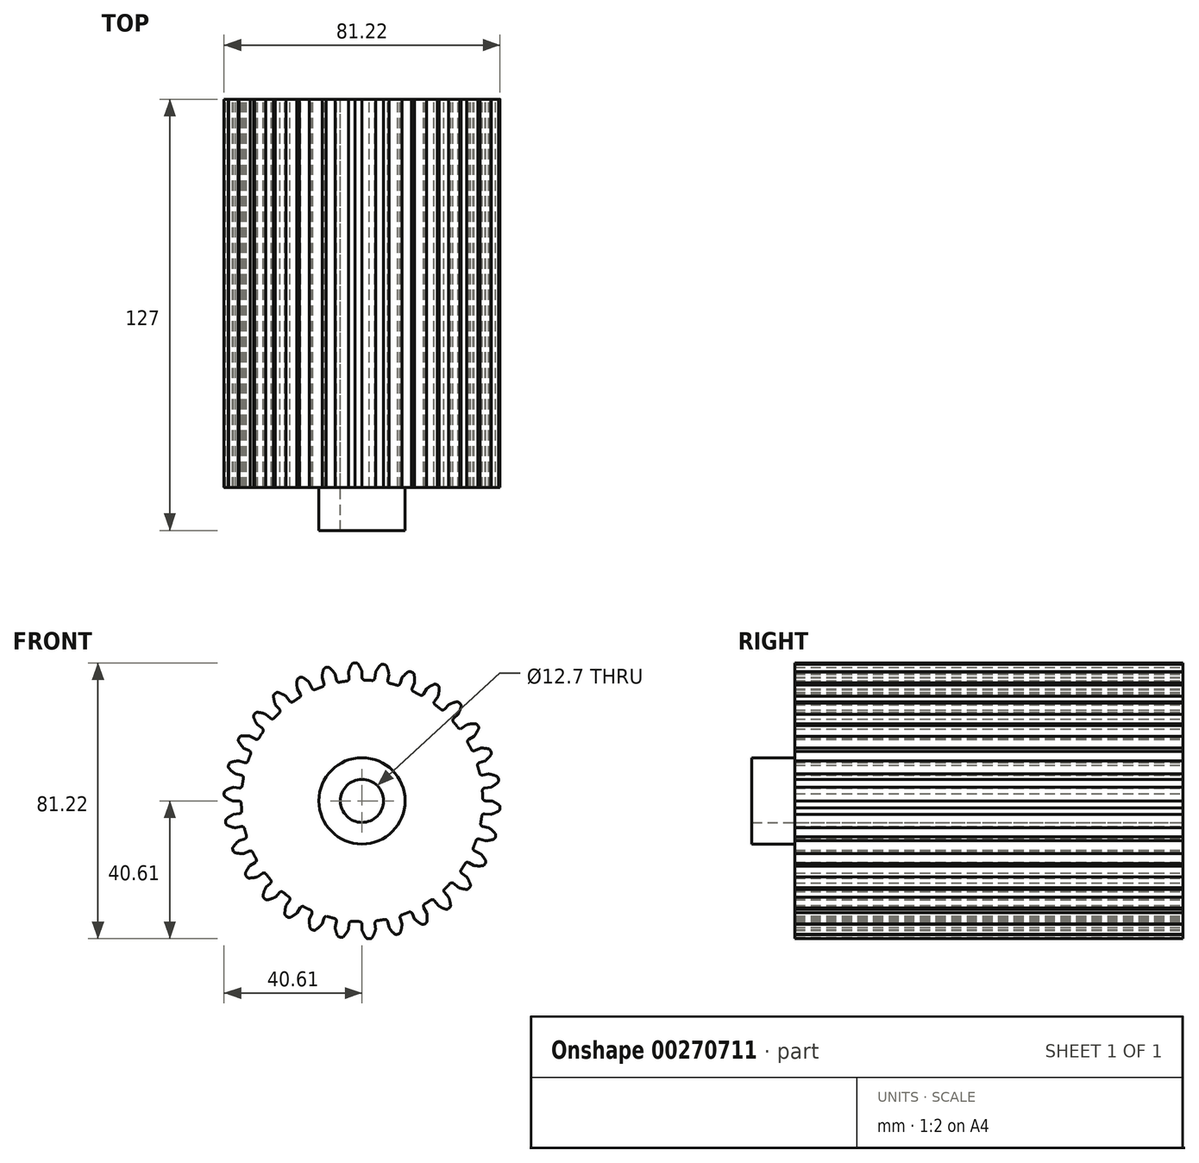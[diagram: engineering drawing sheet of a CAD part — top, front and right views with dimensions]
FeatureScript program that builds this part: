
annotation { "Feature Type Name" : "Feature", "Feature Type Description" : "" }
export const myFeature = defineFeature(function(context is Context, id is Id, definition is map)
    precondition{}
    {
        {
            var Q0;
            Q0=qCreatedBy(makeId("Front.planeOp"),FACE);
            var sketch = newSketch(context, id + "F0", { "sketchPlane" : qUnion([Q0])});
            skArc(sketch, "E0", {"start": v(-4.5, 35.28) * mm, "mid": v(-5.56, 35.12) * mm, "end": v(-6.63, 34.94) * mm});
            skArc(sketch, "E1.trimOffspring", {"start": v(0, 38.1) * mm, "mid": v(-0.52, 39.23) * mm, "end": v(-1.18, 40.3) * mm});
            skLineSegment(sketch, "E2", {"start": v(-1.82, 40.61) * mm, "end": v(-2.13, 40.61) * mm});
            skLineSegment(sketch, "E3", {"start": v(0, 38.1) * mm, "end": v(0, 36.34) * mm});
            skLineSegment(sketch, "E4.MirrorCS", {"start": v(-2.44, 40.58) * mm, "end": v(-2.13, 40.61) * mm});
            skArc(sketch, "E5.MirrorCS", {"start": v(-4, 37.9) * mm, "mid": v(-3.59, 39.07) * mm, "end": v(-3.03, 40.2) * mm});
            skLineSegment(sketch, "E6.MirrorCS", {"start": v(-4, 37.9) * mm, "end": v(-3.8, 36.14) * mm});
            skPoint(sketch, "E7.visualSharp", {"position": v(0, 35.56) * mm});
            skArc(sketch, "E7.filletArc", {"start": v(0, 36.34) * mm, "mid": v(0.23, 35.79) * mm, "end": v(0.78, 35.55) * mm});
            skPoint(sketch, "E8.visualSharp", {"position": v(-1.43, 40.61) * mm});
            skArc(sketch, "E8.filletArc", {"start": v(-1.18, 40.3) * mm, "mid": v(-1.46, 40.53) * mm, "end": v(-1.82, 40.61) * mm});
            skPoint(sketch, "E9.visualSharp", {"position": v(-2.82, 40.54) * mm});
            skArc(sketch, "E9.filletArc", {"start": v(-2.44, 40.58) * mm, "mid": v(-2.78, 40.46) * mm, "end": v(-3.03, 40.2) * mm});
            skPoint(sketch, "E10.visualSharp", {"position": v(-3.73, 35.36) * mm});
            skArc(sketch, "E10.filletArc", {"start": v(-4.5, 35.28) * mm, "mid": v(-3.97, 35.57) * mm, "end": v(-3.8, 36.14) * mm});
            skArc(sketch, "E11.1.0", {"start": v(-11.73, 33.57) * mm, "mid": v(-11.28, 33.96) * mm, "end": v(-11.24, 34.56) * mm});
            skLineSegment(sketch, "E11.1.1", {"start": v(-11.78, 36.23) * mm, "end": v(-11.24, 34.56) * mm});
            skArc(sketch, "E11.1.2", {"start": v(-11.78, 36.23) * mm, "mid": v(-11.63, 37.47) * mm, "end": v(-11.33, 38.68) * mm});
            skArc(sketch, "E11.1.3", {"start": v(-10.82, 39.19) * mm, "mid": v(-11.13, 39) * mm, "end": v(-11.33, 38.68) * mm});
            skLineSegment(sketch, "E11.1.4", {"start": v(-10.82, 39.19) * mm, "end": v(-10.53, 39.28) * mm});
            skLineSegment(sketch, "E11.1.5", {"start": v(-10.22, 39.35) * mm, "end": v(-10.53, 39.28) * mm});
            skArc(sketch, "E11.1.6", {"start": v(-9.53, 39.16) * mm, "mid": v(-9.86, 39.34) * mm, "end": v(-10.22, 39.35) * mm});
            skArc(sketch, "E11.1.7", {"start": v(-7.91, 37.27) * mm, "mid": v(-8.66, 38.27) * mm, "end": v(-9.53, 39.16) * mm});
            skLineSegment(sketch, "E11.1.8", {"start": v(-7.91, 37.27) * mm, "end": v(-7.55, 35.55) * mm});
            skArc(sketch, "E11.1.9", {"start": v(-7.55, 35.55) * mm, "mid": v(-7.21, 35.05) * mm, "end": v(-6.63, 34.94) * mm});
            skArc(sketch, "E11.2.0", {"start": v(-18.45, 30.4) * mm, "mid": v(-18.1, 30.88) * mm, "end": v(-18.18, 31.47) * mm});
            skLineSegment(sketch, "E11.2.1", {"start": v(-19.06, 33) * mm, "end": v(-18.18, 31.47) * mm});
            skArc(sketch, "E11.2.2", {"start": v(-19.06, 33) * mm, "mid": v(-19.17, 34.24) * mm, "end": v(-19.12, 35.48) * mm});
            skArc(sketch, "E11.2.3", {"start": v(-18.73, 36.08) * mm, "mid": v(-19, 35.83) * mm, "end": v(-19.12, 35.48) * mm});
            skLineSegment(sketch, "E11.2.4", {"start": v(-18.73, 36.08) * mm, "end": v(-18.46, 36.24) * mm});
            skLineSegment(sketch, "E11.2.5", {"start": v(-18.18, 36.36) * mm, "end": v(-18.46, 36.24) * mm});
            skArc(sketch, "E11.2.6", {"start": v(-17.47, 36.33) * mm, "mid": v(-17.82, 36.43) * mm, "end": v(-18.18, 36.36) * mm});
            skArc(sketch, "E11.2.7", {"start": v(-15.49, 34.8) * mm, "mid": v(-16.43, 35.63) * mm, "end": v(-17.47, 36.33) * mm});
            skLineSegment(sketch, "E11.2.8", {"start": v(-15.49, 34.8) * mm, "end": v(-14.77, 33.2) * mm});
            skArc(sketch, "E11.2.9", {"start": v(-14.77, 33.2) * mm, "mid": v(-14.34, 32.79) * mm, "end": v(-13.75, 32.8) * mm});
            skArc(sketch, "E11.3.0", {"start": v(-24.37, 25.9) * mm, "mid": v(-24.12, 26.44) * mm, "end": v(-24.32, 27) * mm});
            skLineSegment(sketch, "E11.3.1", {"start": v(-25.5, 28.3) * mm, "end": v(-24.32, 27) * mm});
            skArc(sketch, "E11.3.2", {"start": v(-25.5, 28.3) * mm, "mid": v(-25.87, 29.5) * mm, "end": v(-26.08, 30.73) * mm});
            skArc(sketch, "E11.3.3", {"start": v(-25.82, 31.4) * mm, "mid": v(-26.03, 31.1) * mm, "end": v(-26.08, 30.73) * mm});
            skLineSegment(sketch, "E11.3.4", {"start": v(-25.82, 31.4) * mm, "end": v(-25.6, 31.6) * mm});
            skLineSegment(sketch, "E11.3.5", {"start": v(-25.34, 31.79) * mm, "end": v(-25.6, 31.6) * mm});
            skArc(sketch, "E11.3.6", {"start": v(-24.64, 31.9) * mm, "mid": v(-25, 31.93) * mm, "end": v(-25.34, 31.79) * mm});
            skArc(sketch, "E11.3.7", {"start": v(-22.39, 30.83) * mm, "mid": v(-23.48, 31.44) * mm, "end": v(-24.64, 31.9) * mm});
            skLineSegment(sketch, "E11.3.8", {"start": v(-22.39, 30.83) * mm, "end": v(-21.35, 29.4) * mm});
            skArc(sketch, "E11.3.9", {"start": v(-21.35, 29.4) * mm, "mid": v(-20.85, 29.1) * mm, "end": v(-20.27, 29.22) * mm});
            skArc(sketch, "E11.4.0", {"start": v(-29.22, 20.27) * mm, "mid": v(-29.1, 20.85) * mm, "end": v(-29.4, 21.35) * mm});
            skLineSegment(sketch, "E11.4.1", {"start": v(-30.83, 22.39) * mm, "end": v(-29.4, 21.35) * mm});
            skArc(sketch, "E11.4.2", {"start": v(-30.83, 22.39) * mm, "mid": v(-31.44, 23.48) * mm, "end": v(-31.9, 24.64) * mm});
            skArc(sketch, "E11.4.3", {"start": v(-31.79, 25.34) * mm, "mid": v(-31.93, 25) * mm, "end": v(-31.9, 24.64) * mm});
            skLineSegment(sketch, "E11.4.4", {"start": v(-31.79, 25.34) * mm, "end": v(-31.6, 25.6) * mm});
            skLineSegment(sketch, "E11.4.5", {"start": v(-31.4, 25.82) * mm, "end": v(-31.6, 25.6) * mm});
            skArc(sketch, "E11.4.6", {"start": v(-30.73, 26.08) * mm, "mid": v(-31.1, 26.03) * mm, "end": v(-31.4, 25.82) * mm});
            skArc(sketch, "E11.4.7", {"start": v(-28.3, 25.5) * mm, "mid": v(-29.5, 25.87) * mm, "end": v(-30.73, 26.08) * mm});
            skLineSegment(sketch, "E11.4.8", {"start": v(-28.3, 25.5) * mm, "end": v(-27, 24.32) * mm});
            skArc(sketch, "E11.4.9", {"start": v(-27, 24.32) * mm, "mid": v(-26.44, 24.12) * mm, "end": v(-25.9, 24.37) * mm});
            skArc(sketch, "E11.5.0", {"start": v(-32.8, 13.75) * mm, "mid": v(-32.79, 14.34) * mm, "end": v(-33.2, 14.77) * mm});
            skLineSegment(sketch, "E11.5.1", {"start": v(-34.8, 15.49) * mm, "end": v(-33.2, 14.77) * mm});
            skArc(sketch, "E11.5.2", {"start": v(-34.8, 15.49) * mm, "mid": v(-35.63, 16.43) * mm, "end": v(-36.33, 17.47) * mm});
            skArc(sketch, "E11.5.3", {"start": v(-36.36, 18.18) * mm, "mid": v(-36.43, 17.82) * mm, "end": v(-36.33, 17.47) * mm});
            skLineSegment(sketch, "E11.5.4", {"start": v(-36.36, 18.18) * mm, "end": v(-36.24, 18.46) * mm});
            skLineSegment(sketch, "E11.5.5", {"start": v(-36.08, 18.73) * mm, "end": v(-36.24, 18.46) * mm});
            skArc(sketch, "E11.5.6", {"start": v(-35.48, 19.12) * mm, "mid": v(-35.83, 19) * mm, "end": v(-36.08, 18.73) * mm});
            skArc(sketch, "E11.5.7", {"start": v(-33, 19.06) * mm, "mid": v(-34.24, 19.17) * mm, "end": v(-35.48, 19.12) * mm});
            skLineSegment(sketch, "E11.5.8", {"start": v(-33, 19.06) * mm, "end": v(-31.47, 18.18) * mm});
            skArc(sketch, "E11.5.9", {"start": v(-31.47, 18.18) * mm, "mid": v(-30.88, 18.1) * mm, "end": v(-30.4, 18.45) * mm});
            skArc(sketch, "E11.6.0", {"start": v(-34.94, 6.63) * mm, "mid": v(-35.05, 7.21) * mm, "end": v(-35.55, 7.55) * mm});
            skLineSegment(sketch, "E11.6.1", {"start": v(-37.27, 7.91) * mm, "end": v(-35.55, 7.55) * mm});
            skArc(sketch, "E11.6.2", {"start": v(-37.27, 7.91) * mm, "mid": v(-38.27, 8.66) * mm, "end": v(-39.16, 9.53) * mm});
            skArc(sketch, "E11.6.3", {"start": v(-39.35, 10.22) * mm, "mid": v(-39.34, 9.86) * mm, "end": v(-39.16, 9.53) * mm});
            skLineSegment(sketch, "E11.6.4", {"start": v(-39.35, 10.22) * mm, "end": v(-39.28, 10.53) * mm});
            skLineSegment(sketch, "E11.6.5", {"start": v(-39.19, 10.82) * mm, "end": v(-39.28, 10.53) * mm});
            skArc(sketch, "E11.6.6", {"start": v(-38.68, 11.33) * mm, "mid": v(-39, 11.13) * mm, "end": v(-39.19, 10.82) * mm});
            skArc(sketch, "E11.6.7", {"start": v(-36.23, 11.78) * mm, "mid": v(-37.47, 11.63) * mm, "end": v(-38.68, 11.33) * mm});
            skLineSegment(sketch, "E11.6.8", {"start": v(-36.23, 11.78) * mm, "end": v(-34.56, 11.24) * mm});
            skArc(sketch, "E11.6.9", {"start": v(-34.56, 11.24) * mm, "mid": v(-33.96, 11.28) * mm, "end": v(-33.57, 11.73) * mm});
            skArc(sketch, "E11.7.0", {"start": v(-35.55, -0.78) * mm, "mid": v(-35.79, -0.23) * mm, "end": v(-36.34, 0) * mm});
            skLineSegment(sketch, "E11.7.1", {"start": v(-38.1, 0) * mm, "end": v(-36.34, 0) * mm});
            skArc(sketch, "E11.7.2", {"start": v(-38.1, 0) * mm, "mid": v(-39.23, 0.52) * mm, "end": v(-40.3, 1.18) * mm});
            skArc(sketch, "E11.7.3", {"start": v(-40.61, 1.82) * mm, "mid": v(-40.53, 1.46) * mm, "end": v(-40.3, 1.18) * mm});
            skLineSegment(sketch, "E11.7.4", {"start": v(-40.61, 1.82) * mm, "end": v(-40.61, 2.13) * mm});
            skLineSegment(sketch, "E11.7.5", {"start": v(-40.58, 2.44) * mm, "end": v(-40.61, 2.13) * mm});
            skArc(sketch, "E11.7.6", {"start": v(-40.2, 3.03) * mm, "mid": v(-40.46, 2.78) * mm, "end": v(-40.58, 2.44) * mm});
            skArc(sketch, "E11.7.7", {"start": v(-37.9, 4) * mm, "mid": v(-39.07, 3.59) * mm, "end": v(-40.2, 3.03) * mm});
            skLineSegment(sketch, "E11.7.8", {"start": v(-37.9, 4) * mm, "end": v(-36.14, 3.8) * mm});
            skArc(sketch, "E11.7.9", {"start": v(-36.14, 3.8) * mm, "mid": v(-35.57, 3.97) * mm, "end": v(-35.28, 4.5) * mm});
            skArc(sketch, "E11.8.0", {"start": v(-34.61, -8.15) * mm, "mid": v(-34.96, -7.67) * mm, "end": v(-35.54, -7.56) * mm});
            skLineSegment(sketch, "E11.8.1", {"start": v(-37.27, -7.93) * mm, "end": v(-35.54, -7.56) * mm});
            skArc(sketch, "E11.8.2", {"start": v(-37.27, -7.93) * mm, "mid": v(-38.48, -7.65) * mm, "end": v(-39.66, -7.22) * mm});
            skArc(sketch, "E11.8.3", {"start": v(-40.1, -6.66) * mm, "mid": v(-39.95, -7) * mm, "end": v(-39.66, -7.22) * mm});
            skLineSegment(sketch, "E11.8.4", {"start": v(-40.1, -6.66) * mm, "end": v(-40.17, -6.36) * mm});
            skLineSegment(sketch, "E11.8.5", {"start": v(-40.2, -6.06) * mm, "end": v(-40.17, -6.36) * mm});
            skArc(sketch, "E11.8.6", {"start": v(-39.95, -5.39) * mm, "mid": v(-40.15, -5.7) * mm, "end": v(-40.2, -6.06) * mm});
            skArc(sketch, "E11.8.7", {"start": v(-37.9, -3.97) * mm, "mid": v(-38.97, -4.61) * mm, "end": v(-39.95, -5.39) * mm});
            skLineSegment(sketch, "E11.8.8", {"start": v(-37.9, -3.97) * mm, "end": v(-36.14, -3.79) * mm});
            skArc(sketch, "E11.8.9", {"start": v(-36.14, -3.79) * mm, "mid": v(-35.62, -3.5) * mm, "end": v(-35.44, -2.94) * mm});
            skArc(sketch, "E11.9.0", {"start": v(-32.16, -15.17) * mm, "mid": v(-32.6, -14.77) * mm, "end": v(-33.2, -14.79) * mm});
            skLineSegment(sketch, "E11.9.1", {"start": v(-34.8, -15.5) * mm, "end": v(-33.2, -14.79) * mm});
            skArc(sketch, "E11.9.2", {"start": v(-34.8, -15.5) * mm, "mid": v(-36.05, -15.49) * mm, "end": v(-37.29, -15.3) * mm});
            skArc(sketch, "E11.9.3", {"start": v(-37.84, -14.86) * mm, "mid": v(-37.62, -15.15) * mm, "end": v(-37.29, -15.3) * mm});
            skLineSegment(sketch, "E11.9.4", {"start": v(-37.84, -14.86) * mm, "end": v(-37.97, -14.58) * mm});
            skLineSegment(sketch, "E11.9.5", {"start": v(-38.06, -14.28) * mm, "end": v(-37.97, -14.58) * mm});
            skArc(sketch, "E11.9.6", {"start": v(-37.95, -13.58) * mm, "mid": v(-38.1, -13.92) * mm, "end": v(-38.06, -14.28) * mm});
            skArc(sketch, "E11.9.7", {"start": v(-36.24, -11.77) * mm, "mid": v(-37.16, -12.61) * mm, "end": v(-37.95, -13.58) * mm});
            skLineSegment(sketch, "E11.9.8", {"start": v(-36.24, -11.77) * mm, "end": v(-34.56, -11.22) * mm});
            skArc(sketch, "E11.9.9", {"start": v(-34.56, -11.22) * mm, "mid": v(-34.1, -10.84) * mm, "end": v(-34.05, -10.25) * mm});
            skArc(sketch, "E11.10.0", {"start": v(-28.3, -21.53) * mm, "mid": v(-28.82, -21.22) * mm, "end": v(-29.4, -21.37) * mm});
            skLineSegment(sketch, "E11.10.1", {"start": v(-30.82, -22.4) * mm, "end": v(-29.4, -21.37) * mm});
            skArc(sketch, "E11.10.2", {"start": v(-30.82, -22.4) * mm, "mid": v(-32.04, -22.64) * mm, "end": v(-33.3, -22.73) * mm});
            skArc(sketch, "E11.10.3", {"start": v(-33.93, -22.4) * mm, "mid": v(-33.65, -22.64) * mm, "end": v(-33.3, -22.73) * mm});
            skLineSegment(sketch, "E11.10.4", {"start": v(-33.93, -22.4) * mm, "end": v(-34.1, -22.15) * mm});
            skLineSegment(sketch, "E11.10.5", {"start": v(-34.26, -21.88) * mm, "end": v(-34.1, -22.15) * mm});
            skArc(sketch, "E11.10.6", {"start": v(-34.3, -21.17) * mm, "mid": v(-34.37, -21.53) * mm, "end": v(-34.26, -21.88) * mm});
            skArc(sketch, "E11.10.7", {"start": v(-33, -19.04) * mm, "mid": v(-33.72, -20.06) * mm, "end": v(-34.3, -21.17) * mm});
            skLineSegment(sketch, "E11.10.8", {"start": v(-33, -19.04) * mm, "end": v(-31.47, -18.16) * mm});
            skArc(sketch, "E11.10.9", {"start": v(-31.47, -18.16) * mm, "mid": v(-31.11, -17.7) * mm, "end": v(-31.18, -17.1) * mm});
            skArc(sketch, "E11.11.0", {"start": v(-23.2, -26.94) * mm, "mid": v(-23.77, -26.75) * mm, "end": v(-24.3, -27.01) * mm});
            skLineSegment(sketch, "E11.11.1", {"start": v(-25.49, -28.32) * mm, "end": v(-24.3, -27.01) * mm});
            skArc(sketch, "E11.11.2", {"start": v(-25.49, -28.32) * mm, "mid": v(-26.64, -28.81) * mm, "end": v(-27.84, -29.15) * mm});
            skArc(sketch, "E11.11.3", {"start": v(-28.53, -28.97) * mm, "mid": v(-28.2, -29.14) * mm, "end": v(-27.84, -29.15) * mm});
            skLineSegment(sketch, "E11.11.4", {"start": v(-28.53, -28.97) * mm, "end": v(-28.76, -28.76) * mm});
            skLineSegment(sketch, "E11.11.5", {"start": v(-28.97, -28.53) * mm, "end": v(-28.76, -28.76) * mm});
            skArc(sketch, "E11.11.6", {"start": v(-29.15, -27.84) * mm, "mid": v(-29.14, -28.2) * mm, "end": v(-28.97, -28.53) * mm});
            skArc(sketch, "E11.11.7", {"start": v(-28.32, -25.49) * mm, "mid": v(-28.81, -26.64) * mm, "end": v(-29.15, -27.84) * mm});
            skLineSegment(sketch, "E11.11.8", {"start": v(-28.32, -25.49) * mm, "end": v(-27.01, -24.3) * mm});
            skArc(sketch, "E11.11.9", {"start": v(-27.01, -24.3) * mm, "mid": v(-26.75, -23.77) * mm, "end": v(-26.94, -23.2) * mm});
            skArc(sketch, "E11.12.0", {"start": v(-17.1, -31.18) * mm, "mid": v(-17.7, -31.11) * mm, "end": v(-18.16, -31.47) * mm});
            skLineSegment(sketch, "E11.12.1", {"start": v(-19.04, -33) * mm, "end": v(-18.16, -31.47) * mm});
            skArc(sketch, "E11.12.2", {"start": v(-19.04, -33) * mm, "mid": v(-20.06, -33.72) * mm, "end": v(-21.17, -34.3) * mm});
            skArc(sketch, "E11.12.3", {"start": v(-21.88, -34.26) * mm, "mid": v(-21.53, -34.37) * mm, "end": v(-21.17, -34.3) * mm});
            skLineSegment(sketch, "E11.12.4", {"start": v(-21.88, -34.26) * mm, "end": v(-22.15, -34.1) * mm});
            skLineSegment(sketch, "E11.12.5", {"start": v(-22.4, -33.93) * mm, "end": v(-22.15, -34.1) * mm});
            skArc(sketch, "E11.12.6", {"start": v(-22.73, -33.3) * mm, "mid": v(-22.64, -33.65) * mm, "end": v(-22.4, -33.93) * mm});
            skArc(sketch, "E11.12.7", {"start": v(-22.4, -30.82) * mm, "mid": v(-22.64, -32.04) * mm, "end": v(-22.73, -33.3) * mm});
            skLineSegment(sketch, "E11.12.8", {"start": v(-22.4, -30.82) * mm, "end": v(-21.37, -29.4) * mm});
            skArc(sketch, "E11.12.9", {"start": v(-21.37, -29.4) * mm, "mid": v(-21.22, -28.82) * mm, "end": v(-21.53, -28.3) * mm});
            skArc(sketch, "E11.13.0", {"start": v(-10.25, -34.05) * mm, "mid": v(-10.84, -34.1) * mm, "end": v(-11.22, -34.56) * mm});
            skLineSegment(sketch, "E11.13.1", {"start": v(-11.77, -36.24) * mm, "end": v(-11.22, -34.56) * mm});
            skArc(sketch, "E11.13.2", {"start": v(-11.77, -36.24) * mm, "mid": v(-12.61, -37.16) * mm, "end": v(-13.58, -37.95) * mm});
            skArc(sketch, "E11.13.3", {"start": v(-14.28, -38.06) * mm, "mid": v(-13.92, -38.1) * mm, "end": v(-13.58, -37.95) * mm});
            skLineSegment(sketch, "E11.13.4", {"start": v(-14.28, -38.06) * mm, "end": v(-14.58, -37.97) * mm});
            skLineSegment(sketch, "E11.13.5", {"start": v(-14.86, -37.84) * mm, "end": v(-14.58, -37.97) * mm});
            skArc(sketch, "E11.13.6", {"start": v(-15.3, -37.29) * mm, "mid": v(-15.15, -37.62) * mm, "end": v(-14.86, -37.84) * mm});
            skArc(sketch, "E11.13.7", {"start": v(-15.5, -34.8) * mm, "mid": v(-15.49, -36.05) * mm, "end": v(-15.3, -37.29) * mm});
            skLineSegment(sketch, "E11.13.8", {"start": v(-15.5, -34.8) * mm, "end": v(-14.79, -33.2) * mm});
            skArc(sketch, "E11.13.9", {"start": v(-14.79, -33.2) * mm, "mid": v(-14.77, -32.6) * mm, "end": v(-15.17, -32.16) * mm});
            skArc(sketch, "E11.14.0", {"start": v(-2.94, -35.44) * mm, "mid": v(-3.5, -35.62) * mm, "end": v(-3.79, -36.14) * mm});
            skLineSegment(sketch, "E11.14.1", {"start": v(-3.97, -37.9) * mm, "end": v(-3.79, -36.14) * mm});
            skArc(sketch, "E11.14.2", {"start": v(-3.97, -37.9) * mm, "mid": v(-4.61, -38.97) * mm, "end": v(-5.39, -39.95) * mm});
            skArc(sketch, "E11.14.3", {"start": v(-6.06, -40.2) * mm, "mid": v(-5.7, -40.15) * mm, "end": v(-5.39, -39.95) * mm});
            skLineSegment(sketch, "E11.14.4", {"start": v(-6.06, -40.2) * mm, "end": v(-6.36, -40.17) * mm});
            skLineSegment(sketch, "E11.14.5", {"start": v(-6.66, -40.1) * mm, "end": v(-6.36, -40.17) * mm});
            skArc(sketch, "E11.14.6", {"start": v(-7.22, -39.66) * mm, "mid": v(-7, -39.95) * mm, "end": v(-6.66, -40.1) * mm});
            skArc(sketch, "E11.14.7", {"start": v(-7.93, -37.27) * mm, "mid": v(-7.65, -38.48) * mm, "end": v(-7.22, -39.66) * mm});
            skLineSegment(sketch, "E11.14.8", {"start": v(-7.93, -37.27) * mm, "end": v(-7.56, -35.54) * mm});
            skArc(sketch, "E11.14.9", {"start": v(-7.56, -35.54) * mm, "mid": v(-7.67, -34.96) * mm, "end": v(-8.15, -34.61) * mm});
            skArc(sketch, "E11.15.0", {"start": v(4.5, -35.28) * mm, "mid": v(3.97, -35.57) * mm, "end": v(3.8, -36.14) * mm});
            skLineSegment(sketch, "E11.15.1", {"start": v(4, -37.9) * mm, "end": v(3.8, -36.14) * mm});
            skArc(sketch, "E11.15.2", {"start": v(4, -37.9) * mm, "mid": v(3.59, -39.07) * mm, "end": v(3.03, -40.2) * mm});
            skArc(sketch, "E11.15.3", {"start": v(2.44, -40.58) * mm, "mid": v(2.78, -40.46) * mm, "end": v(3.03, -40.2) * mm});
            skLineSegment(sketch, "E11.15.4", {"start": v(2.44, -40.58) * mm, "end": v(2.13, -40.61) * mm});
            skLineSegment(sketch, "E11.15.5", {"start": v(1.82, -40.61) * mm, "end": v(2.13, -40.61) * mm});
            skArc(sketch, "E11.15.6", {"start": v(1.18, -40.3) * mm, "mid": v(1.46, -40.53) * mm, "end": v(1.82, -40.61) * mm});
            skArc(sketch, "E11.15.7", {"start": v(0, -38.1) * mm, "mid": v(0.52, -39.23) * mm, "end": v(1.18, -40.3) * mm});
            skLineSegment(sketch, "E11.15.8", {"start": v(0, -38.1) * mm, "end": v(0, -36.34) * mm});
            skArc(sketch, "E11.15.9", {"start": v(0, -36.34) * mm, "mid": v(-0.23, -35.79) * mm, "end": v(-0.78, -35.55) * mm});
            skArc(sketch, "E11.16.0", {"start": v(11.73, -33.57) * mm, "mid": v(11.28, -33.96) * mm, "end": v(11.24, -34.56) * mm});
            skLineSegment(sketch, "E11.16.1", {"start": v(11.78, -36.23) * mm, "end": v(11.24, -34.56) * mm});
            skArc(sketch, "E11.16.2", {"start": v(11.78, -36.23) * mm, "mid": v(11.63, -37.47) * mm, "end": v(11.33, -38.68) * mm});
            skArc(sketch, "E11.16.3", {"start": v(10.82, -39.19) * mm, "mid": v(11.13, -39) * mm, "end": v(11.33, -38.68) * mm});
            skLineSegment(sketch, "E11.16.4", {"start": v(10.82, -39.19) * mm, "end": v(10.53, -39.28) * mm});
            skLineSegment(sketch, "E11.16.5", {"start": v(10.22, -39.35) * mm, "end": v(10.53, -39.28) * mm});
            skArc(sketch, "E11.16.6", {"start": v(9.53, -39.16) * mm, "mid": v(9.86, -39.34) * mm, "end": v(10.22, -39.35) * mm});
            skArc(sketch, "E11.16.7", {"start": v(7.91, -37.27) * mm, "mid": v(8.66, -38.27) * mm, "end": v(9.53, -39.16) * mm});
            skLineSegment(sketch, "E11.16.8", {"start": v(7.91, -37.27) * mm, "end": v(7.55, -35.55) * mm});
            skArc(sketch, "E11.16.9", {"start": v(7.55, -35.55) * mm, "mid": v(7.21, -35.05) * mm, "end": v(6.63, -34.94) * mm});
            skArc(sketch, "E11.17.0", {"start": v(18.45, -30.4) * mm, "mid": v(18.1, -30.88) * mm, "end": v(18.18, -31.47) * mm});
            skLineSegment(sketch, "E11.17.1", {"start": v(19.06, -33) * mm, "end": v(18.18, -31.47) * mm});
            skArc(sketch, "E11.17.2", {"start": v(19.06, -33) * mm, "mid": v(19.17, -34.24) * mm, "end": v(19.12, -35.48) * mm});
            skArc(sketch, "E11.17.3", {"start": v(18.73, -36.08) * mm, "mid": v(19, -35.83) * mm, "end": v(19.12, -35.48) * mm});
            skLineSegment(sketch, "E11.17.4", {"start": v(18.73, -36.08) * mm, "end": v(18.46, -36.24) * mm});
            skLineSegment(sketch, "E11.17.5", {"start": v(18.18, -36.36) * mm, "end": v(18.46, -36.24) * mm});
            skArc(sketch, "E11.17.6", {"start": v(17.47, -36.33) * mm, "mid": v(17.82, -36.43) * mm, "end": v(18.18, -36.36) * mm});
            skArc(sketch, "E11.17.7", {"start": v(15.49, -34.8) * mm, "mid": v(16.43, -35.63) * mm, "end": v(17.47, -36.33) * mm});
            skLineSegment(sketch, "E11.17.8", {"start": v(15.49, -34.8) * mm, "end": v(14.77, -33.2) * mm});
            skArc(sketch, "E11.17.9", {"start": v(14.77, -33.2) * mm, "mid": v(14.34, -32.79) * mm, "end": v(13.75, -32.8) * mm});
            skArc(sketch, "E11.18.0", {"start": v(24.37, -25.9) * mm, "mid": v(24.12, -26.44) * mm, "end": v(24.32, -27) * mm});
            skLineSegment(sketch, "E11.18.1", {"start": v(25.5, -28.3) * mm, "end": v(24.32, -27) * mm});
            skArc(sketch, "E11.18.2", {"start": v(25.5, -28.3) * mm, "mid": v(25.87, -29.5) * mm, "end": v(26.08, -30.73) * mm});
            skArc(sketch, "E11.18.3", {"start": v(25.82, -31.4) * mm, "mid": v(26.03, -31.1) * mm, "end": v(26.08, -30.73) * mm});
            skLineSegment(sketch, "E11.18.4", {"start": v(25.82, -31.4) * mm, "end": v(25.6, -31.6) * mm});
            skLineSegment(sketch, "E11.18.5", {"start": v(25.34, -31.79) * mm, "end": v(25.6, -31.6) * mm});
            skArc(sketch, "E11.18.6", {"start": v(24.64, -31.9) * mm, "mid": v(25, -31.93) * mm, "end": v(25.34, -31.79) * mm});
            skArc(sketch, "E11.18.7", {"start": v(22.39, -30.83) * mm, "mid": v(23.48, -31.44) * mm, "end": v(24.64, -31.9) * mm});
            skLineSegment(sketch, "E11.18.8", {"start": v(22.39, -30.83) * mm, "end": v(21.35, -29.4) * mm});
            skArc(sketch, "E11.18.9", {"start": v(21.35, -29.4) * mm, "mid": v(20.85, -29.1) * mm, "end": v(20.27, -29.22) * mm});
            skArc(sketch, "E11.19.0", {"start": v(29.22, -20.27) * mm, "mid": v(29.1, -20.85) * mm, "end": v(29.4, -21.35) * mm});
            skLineSegment(sketch, "E11.19.1", {"start": v(30.83, -22.39) * mm, "end": v(29.4, -21.35) * mm});
            skArc(sketch, "E11.19.2", {"start": v(30.83, -22.39) * mm, "mid": v(31.44, -23.48) * mm, "end": v(31.9, -24.64) * mm});
            skArc(sketch, "E11.19.3", {"start": v(31.79, -25.34) * mm, "mid": v(31.93, -25) * mm, "end": v(31.9, -24.64) * mm});
            skLineSegment(sketch, "E11.19.4", {"start": v(31.79, -25.34) * mm, "end": v(31.6, -25.6) * mm});
            skLineSegment(sketch, "E11.19.5", {"start": v(31.4, -25.82) * mm, "end": v(31.6, -25.6) * mm});
            skArc(sketch, "E11.19.6", {"start": v(30.73, -26.08) * mm, "mid": v(31.1, -26.03) * mm, "end": v(31.4, -25.82) * mm});
            skArc(sketch, "E11.19.7", {"start": v(28.3, -25.5) * mm, "mid": v(29.5, -25.87) * mm, "end": v(30.73, -26.08) * mm});
            skLineSegment(sketch, "E11.19.8", {"start": v(28.3, -25.5) * mm, "end": v(27, -24.32) * mm});
            skArc(sketch, "E11.19.9", {"start": v(27, -24.32) * mm, "mid": v(26.44, -24.12) * mm, "end": v(25.9, -24.37) * mm});
            skArc(sketch, "E11.20.0", {"start": v(32.8, -13.75) * mm, "mid": v(32.79, -14.34) * mm, "end": v(33.2, -14.77) * mm});
            skLineSegment(sketch, "E11.20.1", {"start": v(34.8, -15.49) * mm, "end": v(33.2, -14.77) * mm});
            skArc(sketch, "E11.20.2", {"start": v(34.8, -15.49) * mm, "mid": v(35.63, -16.43) * mm, "end": v(36.33, -17.47) * mm});
            skArc(sketch, "E11.20.3", {"start": v(36.36, -18.18) * mm, "mid": v(36.43, -17.82) * mm, "end": v(36.33, -17.47) * mm});
            skLineSegment(sketch, "E11.20.4", {"start": v(36.36, -18.18) * mm, "end": v(36.24, -18.46) * mm});
            skLineSegment(sketch, "E11.20.5", {"start": v(36.08, -18.73) * mm, "end": v(36.24, -18.46) * mm});
            skArc(sketch, "E11.20.6", {"start": v(35.48, -19.12) * mm, "mid": v(35.83, -19) * mm, "end": v(36.08, -18.73) * mm});
            skArc(sketch, "E11.20.7", {"start": v(33, -19.06) * mm, "mid": v(34.24, -19.17) * mm, "end": v(35.48, -19.12) * mm});
            skLineSegment(sketch, "E11.20.8", {"start": v(33, -19.06) * mm, "end": v(31.47, -18.18) * mm});
            skArc(sketch, "E11.20.9", {"start": v(31.47, -18.18) * mm, "mid": v(30.88, -18.1) * mm, "end": v(30.4, -18.45) * mm});
            skArc(sketch, "E11.21.0", {"start": v(34.94, -6.63) * mm, "mid": v(35.05, -7.21) * mm, "end": v(35.55, -7.55) * mm});
            skLineSegment(sketch, "E11.21.1", {"start": v(37.27, -7.91) * mm, "end": v(35.55, -7.55) * mm});
            skArc(sketch, "E11.21.2", {"start": v(37.27, -7.91) * mm, "mid": v(38.27, -8.66) * mm, "end": v(39.16, -9.53) * mm});
            skArc(sketch, "E11.21.3", {"start": v(39.35, -10.22) * mm, "mid": v(39.34, -9.86) * mm, "end": v(39.16, -9.53) * mm});
            skLineSegment(sketch, "E11.21.4", {"start": v(39.35, -10.22) * mm, "end": v(39.28, -10.53) * mm});
            skLineSegment(sketch, "E11.21.5", {"start": v(39.19, -10.82) * mm, "end": v(39.28, -10.53) * mm});
            skArc(sketch, "E11.21.6", {"start": v(38.68, -11.33) * mm, "mid": v(39, -11.13) * mm, "end": v(39.19, -10.82) * mm});
            skArc(sketch, "E11.21.7", {"start": v(36.23, -11.78) * mm, "mid": v(37.47, -11.63) * mm, "end": v(38.68, -11.33) * mm});
            skLineSegment(sketch, "E11.21.8", {"start": v(36.23, -11.78) * mm, "end": v(34.56, -11.24) * mm});
            skArc(sketch, "E11.21.9", {"start": v(34.56, -11.24) * mm, "mid": v(33.96, -11.28) * mm, "end": v(33.57, -11.73) * mm});
            skArc(sketch, "E11.22.0", {"start": v(35.55, 0.78) * mm, "mid": v(35.79, 0.23) * mm, "end": v(36.34, 0) * mm});
            skLineSegment(sketch, "E11.22.1", {"start": v(38.1, 0) * mm, "end": v(36.34, 0) * mm});
            skArc(sketch, "E11.22.2", {"start": v(38.1, 0) * mm, "mid": v(39.23, -0.52) * mm, "end": v(40.3, -1.18) * mm});
            skArc(sketch, "E11.22.3", {"start": v(40.61, -1.82) * mm, "mid": v(40.53, -1.46) * mm, "end": v(40.3, -1.18) * mm});
            skLineSegment(sketch, "E11.22.4", {"start": v(40.61, -1.82) * mm, "end": v(40.61, -2.13) * mm});
            skLineSegment(sketch, "E11.22.5", {"start": v(40.58, -2.44) * mm, "end": v(40.61, -2.13) * mm});
            skArc(sketch, "E11.22.6", {"start": v(40.2, -3.03) * mm, "mid": v(40.46, -2.78) * mm, "end": v(40.58, -2.44) * mm});
            skArc(sketch, "E11.22.7", {"start": v(37.9, -4) * mm, "mid": v(39.07, -3.59) * mm, "end": v(40.2, -3.03) * mm});
            skLineSegment(sketch, "E11.22.8", {"start": v(37.9, -4) * mm, "end": v(36.14, -3.8) * mm});
            skArc(sketch, "E11.22.9", {"start": v(36.14, -3.8) * mm, "mid": v(35.57, -3.97) * mm, "end": v(35.28, -4.5) * mm});
            skArc(sketch, "E11.23.0", {"start": v(34.61, 8.15) * mm, "mid": v(34.96, 7.67) * mm, "end": v(35.54, 7.56) * mm});
            skLineSegment(sketch, "E11.23.1", {"start": v(37.27, 7.93) * mm, "end": v(35.54, 7.56) * mm});
            skArc(sketch, "E11.23.2", {"start": v(37.27, 7.93) * mm, "mid": v(38.48, 7.65) * mm, "end": v(39.66, 7.22) * mm});
            skArc(sketch, "E11.23.3", {"start": v(40.1, 6.66) * mm, "mid": v(39.95, 7) * mm, "end": v(39.66, 7.22) * mm});
            skLineSegment(sketch, "E11.23.4", {"start": v(40.1, 6.66) * mm, "end": v(40.17, 6.36) * mm});
            skLineSegment(sketch, "E11.23.5", {"start": v(40.2, 6.06) * mm, "end": v(40.17, 6.36) * mm});
            skArc(sketch, "E11.23.6", {"start": v(39.95, 5.39) * mm, "mid": v(40.15, 5.7) * mm, "end": v(40.2, 6.06) * mm});
            skArc(sketch, "E11.23.7", {"start": v(37.9, 3.97) * mm, "mid": v(38.97, 4.61) * mm, "end": v(39.95, 5.39) * mm});
            skLineSegment(sketch, "E11.23.8", {"start": v(37.9, 3.97) * mm, "end": v(36.14, 3.79) * mm});
            skArc(sketch, "E11.23.9", {"start": v(36.14, 3.79) * mm, "mid": v(35.62, 3.5) * mm, "end": v(35.44, 2.94) * mm});
            skArc(sketch, "E11.24.0", {"start": v(32.16, 15.17) * mm, "mid": v(32.6, 14.77) * mm, "end": v(33.2, 14.79) * mm});
            skLineSegment(sketch, "E11.24.1", {"start": v(34.8, 15.5) * mm, "end": v(33.2, 14.79) * mm});
            skArc(sketch, "E11.24.2", {"start": v(34.8, 15.5) * mm, "mid": v(36.05, 15.49) * mm, "end": v(37.29, 15.3) * mm});
            skArc(sketch, "E11.24.3", {"start": v(37.84, 14.86) * mm, "mid": v(37.62, 15.15) * mm, "end": v(37.29, 15.3) * mm});
            skLineSegment(sketch, "E11.24.4", {"start": v(37.84, 14.86) * mm, "end": v(37.97, 14.58) * mm});
            skLineSegment(sketch, "E11.24.5", {"start": v(38.06, 14.28) * mm, "end": v(37.97, 14.58) * mm});
            skArc(sketch, "E11.24.6", {"start": v(37.95, 13.58) * mm, "mid": v(38.1, 13.92) * mm, "end": v(38.06, 14.28) * mm});
            skArc(sketch, "E11.24.7", {"start": v(36.24, 11.77) * mm, "mid": v(37.16, 12.61) * mm, "end": v(37.95, 13.58) * mm});
            skLineSegment(sketch, "E11.24.8", {"start": v(36.24, 11.77) * mm, "end": v(34.56, 11.22) * mm});
            skArc(sketch, "E11.24.9", {"start": v(34.56, 11.22) * mm, "mid": v(34.1, 10.84) * mm, "end": v(34.05, 10.25) * mm});
            skArc(sketch, "E11.25.0", {"start": v(28.3, 21.53) * mm, "mid": v(28.82, 21.22) * mm, "end": v(29.4, 21.37) * mm});
            skLineSegment(sketch, "E11.25.1", {"start": v(30.82, 22.4) * mm, "end": v(29.4, 21.37) * mm});
            skArc(sketch, "E11.25.2", {"start": v(30.82, 22.4) * mm, "mid": v(32.04, 22.64) * mm, "end": v(33.3, 22.73) * mm});
            skArc(sketch, "E11.25.3", {"start": v(33.93, 22.4) * mm, "mid": v(33.65, 22.64) * mm, "end": v(33.3, 22.73) * mm});
            skLineSegment(sketch, "E11.25.4", {"start": v(33.93, 22.4) * mm, "end": v(34.1, 22.15) * mm});
            skLineSegment(sketch, "E11.25.5", {"start": v(34.26, 21.88) * mm, "end": v(34.1, 22.15) * mm});
            skArc(sketch, "E11.25.6", {"start": v(34.3, 21.17) * mm, "mid": v(34.37, 21.53) * mm, "end": v(34.26, 21.88) * mm});
            skArc(sketch, "E11.25.7", {"start": v(33, 19.04) * mm, "mid": v(33.72, 20.06) * mm, "end": v(34.3, 21.17) * mm});
            skLineSegment(sketch, "E11.25.8", {"start": v(33, 19.04) * mm, "end": v(31.47, 18.16) * mm});
            skArc(sketch, "E11.25.9", {"start": v(31.47, 18.16) * mm, "mid": v(31.11, 17.7) * mm, "end": v(31.18, 17.1) * mm});
            skArc(sketch, "E11.26.0", {"start": v(23.2, 26.94) * mm, "mid": v(23.77, 26.75) * mm, "end": v(24.3, 27.01) * mm});
            skLineSegment(sketch, "E11.26.1", {"start": v(25.49, 28.32) * mm, "end": v(24.3, 27.01) * mm});
            skArc(sketch, "E11.26.2", {"start": v(25.49, 28.32) * mm, "mid": v(26.64, 28.81) * mm, "end": v(27.84, 29.15) * mm});
            skArc(sketch, "E11.26.3", {"start": v(28.53, 28.97) * mm, "mid": v(28.2, 29.14) * mm, "end": v(27.84, 29.15) * mm});
            skLineSegment(sketch, "E11.26.4", {"start": v(28.53, 28.97) * mm, "end": v(28.76, 28.76) * mm});
            skLineSegment(sketch, "E11.26.5", {"start": v(28.97, 28.53) * mm, "end": v(28.76, 28.76) * mm});
            skArc(sketch, "E11.26.6", {"start": v(29.15, 27.84) * mm, "mid": v(29.14, 28.2) * mm, "end": v(28.97, 28.53) * mm});
            skArc(sketch, "E11.26.7", {"start": v(28.32, 25.49) * mm, "mid": v(28.81, 26.64) * mm, "end": v(29.15, 27.84) * mm});
            skLineSegment(sketch, "E11.26.8", {"start": v(28.32, 25.49) * mm, "end": v(27.01, 24.3) * mm});
            skArc(sketch, "E11.26.9", {"start": v(27.01, 24.3) * mm, "mid": v(26.75, 23.77) * mm, "end": v(26.94, 23.2) * mm});
            skArc(sketch, "E11.27.0", {"start": v(17.1, 31.18) * mm, "mid": v(17.7, 31.11) * mm, "end": v(18.16, 31.47) * mm});
            skLineSegment(sketch, "E11.27.1", {"start": v(19.04, 33) * mm, "end": v(18.16, 31.47) * mm});
            skArc(sketch, "E11.27.2", {"start": v(19.04, 33) * mm, "mid": v(20.06, 33.72) * mm, "end": v(21.17, 34.3) * mm});
            skArc(sketch, "E11.27.3", {"start": v(21.88, 34.26) * mm, "mid": v(21.53, 34.37) * mm, "end": v(21.17, 34.3) * mm});
            skLineSegment(sketch, "E11.27.4", {"start": v(21.88, 34.26) * mm, "end": v(22.15, 34.1) * mm});
            skLineSegment(sketch, "E11.27.5", {"start": v(22.4, 33.93) * mm, "end": v(22.15, 34.1) * mm});
            skArc(sketch, "E11.27.6", {"start": v(22.73, 33.3) * mm, "mid": v(22.64, 33.65) * mm, "end": v(22.4, 33.93) * mm});
            skArc(sketch, "E11.27.7", {"start": v(22.4, 30.82) * mm, "mid": v(22.64, 32.04) * mm, "end": v(22.73, 33.3) * mm});
            skLineSegment(sketch, "E11.27.8", {"start": v(22.4, 30.82) * mm, "end": v(21.37, 29.4) * mm});
            skArc(sketch, "E11.27.9", {"start": v(21.37, 29.4) * mm, "mid": v(21.22, 28.82) * mm, "end": v(21.53, 28.3) * mm});
            skArc(sketch, "E11.28.0", {"start": v(10.25, 34.05) * mm, "mid": v(10.84, 34.1) * mm, "end": v(11.22, 34.56) * mm});
            skLineSegment(sketch, "E11.28.1", {"start": v(11.77, 36.24) * mm, "end": v(11.22, 34.56) * mm});
            skArc(sketch, "E11.28.2", {"start": v(11.77, 36.24) * mm, "mid": v(12.61, 37.16) * mm, "end": v(13.58, 37.95) * mm});
            skArc(sketch, "E11.28.3", {"start": v(14.28, 38.06) * mm, "mid": v(13.92, 38.1) * mm, "end": v(13.58, 37.95) * mm});
            skLineSegment(sketch, "E11.28.4", {"start": v(14.28, 38.06) * mm, "end": v(14.58, 37.97) * mm});
            skLineSegment(sketch, "E11.28.5", {"start": v(14.86, 37.84) * mm, "end": v(14.58, 37.97) * mm});
            skArc(sketch, "E11.28.6", {"start": v(15.3, 37.29) * mm, "mid": v(15.15, 37.62) * mm, "end": v(14.86, 37.84) * mm});
            skArc(sketch, "E11.28.7", {"start": v(15.5, 34.8) * mm, "mid": v(15.49, 36.05) * mm, "end": v(15.3, 37.29) * mm});
            skLineSegment(sketch, "E11.28.8", {"start": v(15.5, 34.8) * mm, "end": v(14.79, 33.2) * mm});
            skArc(sketch, "E11.28.9", {"start": v(14.79, 33.2) * mm, "mid": v(14.77, 32.6) * mm, "end": v(15.17, 32.16) * mm});
            skArc(sketch, "E11.29.0", {"start": v(2.94, 35.44) * mm, "mid": v(3.5, 35.62) * mm, "end": v(3.79, 36.14) * mm});
            skLineSegment(sketch, "E11.29.1", {"start": v(3.97, 37.9) * mm, "end": v(3.79, 36.14) * mm});
            skArc(sketch, "E11.29.2", {"start": v(3.97, 37.9) * mm, "mid": v(4.61, 38.97) * mm, "end": v(5.39, 39.95) * mm});
            skArc(sketch, "E11.29.3", {"start": v(6.06, 40.2) * mm, "mid": v(5.7, 40.15) * mm, "end": v(5.39, 39.95) * mm});
            skLineSegment(sketch, "E11.29.4", {"start": v(6.06, 40.2) * mm, "end": v(6.36, 40.17) * mm});
            skLineSegment(sketch, "E11.29.5", {"start": v(6.66, 40.1) * mm, "end": v(6.36, 40.17) * mm});
            skArc(sketch, "E11.29.6", {"start": v(7.22, 39.66) * mm, "mid": v(7, 39.95) * mm, "end": v(6.66, 40.1) * mm});
            skArc(sketch, "E11.29.7", {"start": v(7.93, 37.27) * mm, "mid": v(7.65, 38.48) * mm, "end": v(7.22, 39.66) * mm});
            skLineSegment(sketch, "E11.29.8", {"start": v(7.93, 37.27) * mm, "end": v(7.56, 35.54) * mm});
            skArc(sketch, "E11.29.9", {"start": v(7.56, 35.54) * mm, "mid": v(7.67, 34.96) * mm, "end": v(8.15, 34.61) * mm});
            skArc(sketch, "E12.trimOffspring", {"start": v(2.94, 35.44) * mm, "mid": v(1.86, 35.51) * mm, "end": v(0.78, 35.55) * mm});
            skArc(sketch, "E13.trimOffspring", {"start": v(10.25, 34.05) * mm, "mid": v(9.2, 34.35) * mm, "end": v(8.15, 34.61) * mm});
            skArc(sketch, "E14.trimOffspring", {"start": v(17.1, 31.18) * mm, "mid": v(16.14, 31.68) * mm, "end": v(15.17, 32.16) * mm});
            skArc(sketch, "E15.trimOffspring", {"start": v(23.2, 26.94) * mm, "mid": v(22.38, 27.64) * mm, "end": v(21.53, 28.3) * mm});
            skArc(sketch, "E16.trimOffspring", {"start": v(28.3, 21.53) * mm, "mid": v(27.64, 22.38) * mm, "end": v(26.94, 23.2) * mm});
            skArc(sketch, "E17.trimOffspring", {"start": v(32.16, 15.17) * mm, "mid": v(31.68, 16.14) * mm, "end": v(31.18, 17.1) * mm});
            skArc(sketch, "E18.trimOffspring", {"start": v(34.61, 8.15) * mm, "mid": v(34.35, 9.2) * mm, "end": v(34.05, 10.25) * mm});
            skArc(sketch, "E19.trimOffspring", {"start": v(35.55, 0.78) * mm, "mid": v(35.51, 1.86) * mm, "end": v(35.44, 2.94) * mm});
            skArc(sketch, "E20.trimOffspring", {"start": v(34.94, -6.63) * mm, "mid": v(35.12, -5.56) * mm, "end": v(35.28, -4.5) * mm});
            skArc(sketch, "E21.trimOffspring", {"start": v(32.8, -13.75) * mm, "mid": v(33.2, -12.74) * mm, "end": v(33.57, -11.73) * mm});
            skArc(sketch, "E22.trimOffspring", {"start": v(29.22, -20.27) * mm, "mid": v(29.82, -19.37) * mm, "end": v(30.4, -18.45) * mm});
            skArc(sketch, "E23.trimOffspring", {"start": v(24.37, -25.9) * mm, "mid": v(25.14, -25.14) * mm, "end": v(25.9, -24.37) * mm});
            skArc(sketch, "E24.trimOffspring", {"start": v(18.45, -30.4) * mm, "mid": v(19.37, -29.82) * mm, "end": v(20.27, -29.22) * mm});
            skArc(sketch, "E25.trimOffspring", {"start": v(11.73, -33.57) * mm, "mid": v(12.74, -33.2) * mm, "end": v(13.75, -32.8) * mm});
            skArc(sketch, "E26.trimOffspring", {"start": v(4.5, -35.28) * mm, "mid": v(5.56, -35.12) * mm, "end": v(6.63, -34.94) * mm});
            skArc(sketch, "E27.trimOffspring", {"start": v(-2.94, -35.44) * mm, "mid": v(-1.86, -35.51) * mm, "end": v(-0.78, -35.55) * mm});
            skArc(sketch, "E28.trimOffspring", {"start": v(-10.25, -34.05) * mm, "mid": v(-9.2, -34.35) * mm, "end": v(-8.15, -34.61) * mm});
            skArc(sketch, "E29.trimOffspring", {"start": v(-17.1, -31.18) * mm, "mid": v(-16.14, -31.68) * mm, "end": v(-15.17, -32.16) * mm});
            skArc(sketch, "E30.trimOffspring", {"start": v(-23.2, -26.94) * mm, "mid": v(-22.38, -27.64) * mm, "end": v(-21.53, -28.3) * mm});
            skArc(sketch, "E31.trimOffspring", {"start": v(-32.16, -15.17) * mm, "mid": v(-29.82, -19.37) * mm, "end": v(-26.94, -23.2) * mm});
            skArc(sketch, "E32.trimOffspring", {"start": v(-34.61, -8.15) * mm, "mid": v(-34.35, -9.2) * mm, "end": v(-34.05, -10.25) * mm});
            skArc(sketch, "E33.trimOffspring", {"start": v(-35.55, -0.78) * mm, "mid": v(-35.51, -1.86) * mm, "end": v(-35.44, -2.94) * mm});
            skArc(sketch, "E34.trimOffspring", {"start": v(-34.94, 6.63) * mm, "mid": v(-35.12, 5.56) * mm, "end": v(-35.28, 4.5) * mm});
            skArc(sketch, "E35.trimOffspring", {"start": v(-32.8, 13.75) * mm, "mid": v(-33.2, 12.74) * mm, "end": v(-33.57, 11.73) * mm});
            skArc(sketch, "E36.trimOffspring", {"start": v(-29.22, 20.27) * mm, "mid": v(-29.82, 19.37) * mm, "end": v(-30.4, 18.45) * mm});
            skArc(sketch, "E37.trimOffspring", {"start": v(-24.37, 25.9) * mm, "mid": v(-25.14, 25.14) * mm, "end": v(-25.9, 24.37) * mm});
            skArc(sketch, "E38.trimOffspring", {"start": v(-18.45, 30.4) * mm, "mid": v(-19.37, 29.82) * mm, "end": v(-20.27, 29.22) * mm});
            skArc(sketch, "E39.trimOffspring", {"start": v(-11.73, 33.57) * mm, "mid": v(-12.74, 33.2) * mm, "end": v(-13.75, 32.8) * mm});
            skCircle(sketch, "E40", {"center": v(0, 0) * mm, "radius": 6.35 * mm});
            skSolve(sketch);
        }
        {
            var Q0;
            Q0 = qSketchRegion(id + "F0", true);
            extrude(context, id + "F1", {"entities" : qUnion([Q0]), "depth" : 114.3 * mm});
        }
        {
            var Q0;
            Q0=makeQuery(id+"F1.opExtrude","CAP_FACE",FACE,{"disambiguationData":[OSD([sQuery(id+"F0.wireOp",EDGE,"E0"),sQuery(id+"F0.wireOp",EDGE,"E1.trimOffspring"),sQuery(id+"F0.wireOp",EDGE,"E2"),sQuery(id+"F0.wireOp",EDGE,"E3"),sQuery(id+"F0.wireOp",EDGE,"E4.MirrorCS"),sQuery(id+"F0.wireOp",EDGE,"E5.MirrorCS"),sQuery(id+"F0.wireOp",EDGE,"E6.MirrorCS"),sQuery(id+"F0.wireOp",EDGE,"E7.filletArc"),sQuery(id+"F0.wireOp",EDGE,"E8.filletArc"),sQuery(id+"F0.wireOp",EDGE,"E9.filletArc"),sQuery(id+"F0.wireOp",EDGE,"E10.filletArc"),sQuery(id+"F0.wireOp",EDGE,"E11.1.0"),sQuery(id+"F0.wireOp",EDGE,"E11.1.1"),sQuery(id+"F0.wireOp",EDGE,"E11.1.2"),sQuery(id+"F0.wireOp",EDGE,"E11.1.3"),sQuery(id+"F0.wireOp",EDGE,"E11.1.4"),sQuery(id+"F0.wireOp",EDGE,"E11.1.5"),sQuery(id+"F0.wireOp",EDGE,"E11.1.6"),sQuery(id+"F0.wireOp",EDGE,"E11.1.7"),sQuery(id+"F0.wireOp",EDGE,"E11.1.8"),sQuery(id+"F0.wireOp",EDGE,"E11.1.9"),sQuery(id+"F0.wireOp",EDGE,"E11.2.0"),sQuery(id+"F0.wireOp",EDGE,"E11.2.1"),sQuery(id+"F0.wireOp",EDGE,"E11.2.2"),sQuery(id+"F0.wireOp",EDGE,"E11.2.3"),sQuery(id+"F0.wireOp",EDGE,"E11.2.4"),sQuery(id+"F0.wireOp",EDGE,"E11.2.5"),sQuery(id+"F0.wireOp",EDGE,"E11.2.6"),sQuery(id+"F0.wireOp",EDGE,"E11.2.7"),sQuery(id+"F0.wireOp",EDGE,"E11.2.8"),sQuery(id+"F0.wireOp",EDGE,"E11.2.9"),sQuery(id+"F0.wireOp",EDGE,"E11.3.0"),sQuery(id+"F0.wireOp",EDGE,"E11.3.1"),sQuery(id+"F0.wireOp",EDGE,"E11.3.2"),sQuery(id+"F0.wireOp",EDGE,"E11.3.3"),sQuery(id+"F0.wireOp",EDGE,"E11.3.4"),sQuery(id+"F0.wireOp",EDGE,"E11.3.5"),sQuery(id+"F0.wireOp",EDGE,"E11.3.6"),sQuery(id+"F0.wireOp",EDGE,"E11.3.7"),sQuery(id+"F0.wireOp",EDGE,"E11.3.8"),sQuery(id+"F0.wireOp",EDGE,"E11.3.9"),sQuery(id+"F0.wireOp",EDGE,"E11.4.0"),sQuery(id+"F0.wireOp",EDGE,"E11.4.1"),sQuery(id+"F0.wireOp",EDGE,"E11.4.2"),sQuery(id+"F0.wireOp",EDGE,"E11.4.3"),sQuery(id+"F0.wireOp",EDGE,"E11.4.4"),sQuery(id+"F0.wireOp",EDGE,"E11.4.5"),sQuery(id+"F0.wireOp",EDGE,"E11.4.6"),sQuery(id+"F0.wireOp",EDGE,"E11.4.7"),sQuery(id+"F0.wireOp",EDGE,"E11.4.8"),sQuery(id+"F0.wireOp",EDGE,"E11.4.9"),sQuery(id+"F0.wireOp",EDGE,"E11.5.0"),sQuery(id+"F0.wireOp",EDGE,"E11.5.1"),sQuery(id+"F0.wireOp",EDGE,"E11.5.2"),sQuery(id+"F0.wireOp",EDGE,"E11.5.3"),sQuery(id+"F0.wireOp",EDGE,"E11.5.4"),sQuery(id+"F0.wireOp",EDGE,"E11.5.5"),sQuery(id+"F0.wireOp",EDGE,"E11.5.6"),sQuery(id+"F0.wireOp",EDGE,"E11.5.7"),sQuery(id+"F0.wireOp",EDGE,"E11.5.8"),sQuery(id+"F0.wireOp",EDGE,"E11.5.9"),sQuery(id+"F0.wireOp",EDGE,"E11.6.0"),sQuery(id+"F0.wireOp",EDGE,"E11.6.1"),sQuery(id+"F0.wireOp",EDGE,"E11.6.2"),sQuery(id+"F0.wireOp",EDGE,"E11.6.3"),sQuery(id+"F0.wireOp",EDGE,"E11.6.4"),sQuery(id+"F0.wireOp",EDGE,"E11.6.5"),sQuery(id+"F0.wireOp",EDGE,"E11.6.6"),sQuery(id+"F0.wireOp",EDGE,"E11.6.7"),sQuery(id+"F0.wireOp",EDGE,"E11.6.8"),sQuery(id+"F0.wireOp",EDGE,"E11.6.9"),sQuery(id+"F0.wireOp",EDGE,"E11.7.0"),sQuery(id+"F0.wireOp",EDGE,"E11.7.1"),sQuery(id+"F0.wireOp",EDGE,"E11.7.2"),sQuery(id+"F0.wireOp",EDGE,"E11.7.3"),sQuery(id+"F0.wireOp",EDGE,"E11.7.4"),sQuery(id+"F0.wireOp",EDGE,"E11.7.5"),sQuery(id+"F0.wireOp",EDGE,"E11.7.6"),sQuery(id+"F0.wireOp",EDGE,"E11.7.7"),sQuery(id+"F0.wireOp",EDGE,"E11.7.8"),sQuery(id+"F0.wireOp",EDGE,"E11.7.9"),sQuery(id+"F0.wireOp",EDGE,"E11.8.0"),sQuery(id+"F0.wireOp",EDGE,"E11.8.1"),sQuery(id+"F0.wireOp",EDGE,"E11.8.2"),sQuery(id+"F0.wireOp",EDGE,"E11.8.3"),sQuery(id+"F0.wireOp",EDGE,"E11.8.4"),sQuery(id+"F0.wireOp",EDGE,"E11.8.5"),sQuery(id+"F0.wireOp",EDGE,"E11.8.6"),sQuery(id+"F0.wireOp",EDGE,"E11.8.7"),sQuery(id+"F0.wireOp",EDGE,"E11.8.8"),sQuery(id+"F0.wireOp",EDGE,"E11.8.9"),sQuery(id+"F0.wireOp",EDGE,"E11.9.0"),sQuery(id+"F0.wireOp",EDGE,"E11.9.1"),sQuery(id+"F0.wireOp",EDGE,"E11.9.2"),sQuery(id+"F0.wireOp",EDGE,"E11.9.3"),sQuery(id+"F0.wireOp",EDGE,"E11.9.4"),sQuery(id+"F0.wireOp",EDGE,"E11.9.5"),sQuery(id+"F0.wireOp",EDGE,"E11.9.6"),sQuery(id+"F0.wireOp",EDGE,"E11.9.7"),sQuery(id+"F0.wireOp",EDGE,"E11.9.8"),sQuery(id+"F0.wireOp",EDGE,"E11.9.9"),sQuery(id+"F0.wireOp",EDGE,"E11.10.0"),sQuery(id+"F0.wireOp",EDGE,"E11.10.1"),sQuery(id+"F0.wireOp",EDGE,"E11.10.2"),sQuery(id+"F0.wireOp",EDGE,"E11.10.3"),sQuery(id+"F0.wireOp",EDGE,"E11.10.4"),sQuery(id+"F0.wireOp",EDGE,"E11.10.5"),sQuery(id+"F0.wireOp",EDGE,"E11.10.6"),sQuery(id+"F0.wireOp",EDGE,"E11.10.7"),sQuery(id+"F0.wireOp",EDGE,"E11.10.8"),sQuery(id+"F0.wireOp",EDGE,"E11.10.9"),sQuery(id+"F0.wireOp",EDGE,"E11.11.0"),sQuery(id+"F0.wireOp",EDGE,"E11.11.1"),sQuery(id+"F0.wireOp",EDGE,"E11.11.2"),sQuery(id+"F0.wireOp",EDGE,"E11.11.3"),sQuery(id+"F0.wireOp",EDGE,"E11.11.4"),sQuery(id+"F0.wireOp",EDGE,"E11.11.5"),sQuery(id+"F0.wireOp",EDGE,"E11.11.6"),sQuery(id+"F0.wireOp",EDGE,"E11.11.7"),sQuery(id+"F0.wireOp",EDGE,"E11.11.8"),sQuery(id+"F0.wireOp",EDGE,"E11.11.9"),sQuery(id+"F0.wireOp",EDGE,"E11.12.0"),sQuery(id+"F0.wireOp",EDGE,"E11.12.1"),sQuery(id+"F0.wireOp",EDGE,"E11.12.2"),sQuery(id+"F0.wireOp",EDGE,"E11.12.3"),sQuery(id+"F0.wireOp",EDGE,"E11.12.4"),sQuery(id+"F0.wireOp",EDGE,"E11.12.5"),sQuery(id+"F0.wireOp",EDGE,"E11.12.6"),sQuery(id+"F0.wireOp",EDGE,"E11.12.7"),sQuery(id+"F0.wireOp",EDGE,"E11.12.8"),sQuery(id+"F0.wireOp",EDGE,"E11.12.9"),sQuery(id+"F0.wireOp",EDGE,"E11.13.0"),sQuery(id+"F0.wireOp",EDGE,"E11.13.1"),sQuery(id+"F0.wireOp",EDGE,"E11.13.2"),sQuery(id+"F0.wireOp",EDGE,"E11.13.3"),sQuery(id+"F0.wireOp",EDGE,"E11.13.4"),sQuery(id+"F0.wireOp",EDGE,"E11.13.5"),sQuery(id+"F0.wireOp",EDGE,"E11.13.6"),sQuery(id+"F0.wireOp",EDGE,"E11.13.7"),sQuery(id+"F0.wireOp",EDGE,"E11.13.8"),sQuery(id+"F0.wireOp",EDGE,"E11.13.9"),sQuery(id+"F0.wireOp",EDGE,"E11.14.0"),sQuery(id+"F0.wireOp",EDGE,"E11.14.1"),sQuery(id+"F0.wireOp",EDGE,"E11.14.2"),sQuery(id+"F0.wireOp",EDGE,"E11.14.3"),sQuery(id+"F0.wireOp",EDGE,"E11.14.4"),sQuery(id+"F0.wireOp",EDGE,"E11.14.5"),sQuery(id+"F0.wireOp",EDGE,"E11.14.6"),sQuery(id+"F0.wireOp",EDGE,"E11.14.7"),sQuery(id+"F0.wireOp",EDGE,"E11.14.8"),sQuery(id+"F0.wireOp",EDGE,"E11.14.9"),sQuery(id+"F0.wireOp",EDGE,"E11.15.0"),sQuery(id+"F0.wireOp",EDGE,"E11.15.1"),sQuery(id+"F0.wireOp",EDGE,"E11.15.2"),sQuery(id+"F0.wireOp",EDGE,"E11.15.3"),sQuery(id+"F0.wireOp",EDGE,"E11.15.4"),sQuery(id+"F0.wireOp",EDGE,"E11.15.5"),sQuery(id+"F0.wireOp",EDGE,"E11.15.6"),sQuery(id+"F0.wireOp",EDGE,"E11.15.7"),sQuery(id+"F0.wireOp",EDGE,"E11.15.8"),sQuery(id+"F0.wireOp",EDGE,"E11.15.9"),sQuery(id+"F0.wireOp",EDGE,"E11.16.0"),sQuery(id+"F0.wireOp",EDGE,"E11.16.1"),sQuery(id+"F0.wireOp",EDGE,"E11.16.2"),sQuery(id+"F0.wireOp",EDGE,"E11.16.3"),sQuery(id+"F0.wireOp",EDGE,"E11.16.4"),sQuery(id+"F0.wireOp",EDGE,"E11.16.5"),sQuery(id+"F0.wireOp",EDGE,"E11.16.6"),sQuery(id+"F0.wireOp",EDGE,"E11.16.7"),sQuery(id+"F0.wireOp",EDGE,"E11.16.8"),sQuery(id+"F0.wireOp",EDGE,"E11.16.9"),sQuery(id+"F0.wireOp",EDGE,"E11.17.0"),sQuery(id+"F0.wireOp",EDGE,"E11.17.1"),sQuery(id+"F0.wireOp",EDGE,"E11.17.2"),sQuery(id+"F0.wireOp",EDGE,"E11.17.3"),sQuery(id+"F0.wireOp",EDGE,"E11.17.4"),sQuery(id+"F0.wireOp",EDGE,"E11.17.5"),sQuery(id+"F0.wireOp",EDGE,"E11.17.6"),sQuery(id+"F0.wireOp",EDGE,"E11.17.7"),sQuery(id+"F0.wireOp",EDGE,"E11.17.8"),sQuery(id+"F0.wireOp",EDGE,"E11.17.9"),sQuery(id+"F0.wireOp",EDGE,"E11.18.0"),sQuery(id+"F0.wireOp",EDGE,"E11.18.1"),sQuery(id+"F0.wireOp",EDGE,"E11.18.2"),sQuery(id+"F0.wireOp",EDGE,"E11.18.3"),sQuery(id+"F0.wireOp",EDGE,"E11.18.4"),sQuery(id+"F0.wireOp",EDGE,"E11.18.5"),sQuery(id+"F0.wireOp",EDGE,"E11.18.6"),sQuery(id+"F0.wireOp",EDGE,"E11.18.7"),sQuery(id+"F0.wireOp",EDGE,"E11.18.8"),sQuery(id+"F0.wireOp",EDGE,"E11.18.9"),sQuery(id+"F0.wireOp",EDGE,"E11.19.0"),sQuery(id+"F0.wireOp",EDGE,"E11.19.1"),sQuery(id+"F0.wireOp",EDGE,"E11.19.2"),sQuery(id+"F0.wireOp",EDGE,"E11.19.3"),sQuery(id+"F0.wireOp",EDGE,"E11.19.4"),sQuery(id+"F0.wireOp",EDGE,"E11.19.5"),sQuery(id+"F0.wireOp",EDGE,"E11.19.6"),sQuery(id+"F0.wireOp",EDGE,"E11.19.7"),sQuery(id+"F0.wireOp",EDGE,"E11.19.8"),sQuery(id+"F0.wireOp",EDGE,"E11.19.9"),sQuery(id+"F0.wireOp",EDGE,"E11.20.0"),sQuery(id+"F0.wireOp",EDGE,"E11.20.1"),sQuery(id+"F0.wireOp",EDGE,"E11.20.2"),sQuery(id+"F0.wireOp",EDGE,"E11.20.3"),sQuery(id+"F0.wireOp",EDGE,"E11.20.4"),sQuery(id+"F0.wireOp",EDGE,"E11.20.5"),sQuery(id+"F0.wireOp",EDGE,"E11.20.6"),sQuery(id+"F0.wireOp",EDGE,"E11.20.7"),sQuery(id+"F0.wireOp",EDGE,"E11.20.8"),sQuery(id+"F0.wireOp",EDGE,"E11.20.9"),sQuery(id+"F0.wireOp",EDGE,"E11.21.0"),sQuery(id+"F0.wireOp",EDGE,"E11.21.1"),sQuery(id+"F0.wireOp",EDGE,"E11.21.2"),sQuery(id+"F0.wireOp",EDGE,"E11.21.3"),sQuery(id+"F0.wireOp",EDGE,"E11.21.4"),sQuery(id+"F0.wireOp",EDGE,"E11.21.5"),sQuery(id+"F0.wireOp",EDGE,"E11.21.6"),sQuery(id+"F0.wireOp",EDGE,"E11.21.7"),sQuery(id+"F0.wireOp",EDGE,"E11.21.8"),sQuery(id+"F0.wireOp",EDGE,"E11.21.9"),sQuery(id+"F0.wireOp",EDGE,"E11.22.0"),sQuery(id+"F0.wireOp",EDGE,"E11.22.1"),sQuery(id+"F0.wireOp",EDGE,"E11.22.2"),sQuery(id+"F0.wireOp",EDGE,"E11.22.3"),sQuery(id+"F0.wireOp",EDGE,"E11.22.4"),sQuery(id+"F0.wireOp",EDGE,"E11.22.5"),sQuery(id+"F0.wireOp",EDGE,"E11.22.6"),sQuery(id+"F0.wireOp",EDGE,"E11.22.7"),sQuery(id+"F0.wireOp",EDGE,"E11.22.8"),sQuery(id+"F0.wireOp",EDGE,"E11.22.9"),sQuery(id+"F0.wireOp",EDGE,"E11.23.0"),sQuery(id+"F0.wireOp",EDGE,"E11.23.1"),sQuery(id+"F0.wireOp",EDGE,"E11.23.2"),sQuery(id+"F0.wireOp",EDGE,"E11.23.3"),sQuery(id+"F0.wireOp",EDGE,"E11.23.4"),sQuery(id+"F0.wireOp",EDGE,"E11.23.5"),sQuery(id+"F0.wireOp",EDGE,"E11.23.6"),sQuery(id+"F0.wireOp",EDGE,"E11.23.7"),sQuery(id+"F0.wireOp",EDGE,"E11.23.8"),sQuery(id+"F0.wireOp",EDGE,"E11.23.9"),sQuery(id+"F0.wireOp",EDGE,"E11.24.0"),sQuery(id+"F0.wireOp",EDGE,"E11.24.1"),sQuery(id+"F0.wireOp",EDGE,"E11.24.2"),sQuery(id+"F0.wireOp",EDGE,"E11.24.3"),sQuery(id+"F0.wireOp",EDGE,"E11.24.4"),sQuery(id+"F0.wireOp",EDGE,"E11.24.5"),sQuery(id+"F0.wireOp",EDGE,"E11.24.6"),sQuery(id+"F0.wireOp",EDGE,"E11.24.7"),sQuery(id+"F0.wireOp",EDGE,"E11.24.8"),sQuery(id+"F0.wireOp",EDGE,"E11.24.9"),sQuery(id+"F0.wireOp",EDGE,"E11.25.0"),sQuery(id+"F0.wireOp",EDGE,"E11.25.1"),sQuery(id+"F0.wireOp",EDGE,"E11.25.2"),sQuery(id+"F0.wireOp",EDGE,"E11.25.3"),sQuery(id+"F0.wireOp",EDGE,"E11.25.4"),sQuery(id+"F0.wireOp",EDGE,"E11.25.5"),sQuery(id+"F0.wireOp",EDGE,"E11.25.6"),sQuery(id+"F0.wireOp",EDGE,"E11.25.7"),sQuery(id+"F0.wireOp",EDGE,"E11.25.8"),sQuery(id+"F0.wireOp",EDGE,"E11.25.9"),sQuery(id+"F0.wireOp",EDGE,"E11.26.0"),sQuery(id+"F0.wireOp",EDGE,"E11.26.1"),sQuery(id+"F0.wireOp",EDGE,"E11.26.2"),sQuery(id+"F0.wireOp",EDGE,"E11.26.3"),sQuery(id+"F0.wireOp",EDGE,"E11.26.4"),sQuery(id+"F0.wireOp",EDGE,"E11.26.5"),sQuery(id+"F0.wireOp",EDGE,"E11.26.6"),sQuery(id+"F0.wireOp",EDGE,"E11.26.7"),sQuery(id+"F0.wireOp",EDGE,"E11.26.8"),sQuery(id+"F0.wireOp",EDGE,"E11.26.9"),sQuery(id+"F0.wireOp",EDGE,"E11.27.0"),sQuery(id+"F0.wireOp",EDGE,"E11.27.1"),sQuery(id+"F0.wireOp",EDGE,"E11.27.2"),sQuery(id+"F0.wireOp",EDGE,"E11.27.3"),sQuery(id+"F0.wireOp",EDGE,"E11.27.4"),sQuery(id+"F0.wireOp",EDGE,"E11.27.5"),sQuery(id+"F0.wireOp",EDGE,"E11.27.6"),sQuery(id+"F0.wireOp",EDGE,"E11.27.7"),sQuery(id+"F0.wireOp",EDGE,"E11.27.8"),sQuery(id+"F0.wireOp",EDGE,"E11.27.9"),sQuery(id+"F0.wireOp",EDGE,"E11.28.0"),sQuery(id+"F0.wireOp",EDGE,"E11.28.1"),sQuery(id+"F0.wireOp",EDGE,"E11.28.2"),sQuery(id+"F0.wireOp",EDGE,"E11.28.3"),sQuery(id+"F0.wireOp",EDGE,"E11.28.4"),sQuery(id+"F0.wireOp",EDGE,"E11.28.5"),sQuery(id+"F0.wireOp",EDGE,"E11.28.6"),sQuery(id+"F0.wireOp",EDGE,"E11.28.7"),sQuery(id+"F0.wireOp",EDGE,"E11.28.8"),sQuery(id+"F0.wireOp",EDGE,"E11.28.9"),sQuery(id+"F0.wireOp",EDGE,"E11.29.0"),sQuery(id+"F0.wireOp",EDGE,"E11.29.1"),sQuery(id+"F0.wireOp",EDGE,"E11.29.2"),sQuery(id+"F0.wireOp",EDGE,"E11.29.3"),sQuery(id+"F0.wireOp",EDGE,"E11.29.4"),sQuery(id+"F0.wireOp",EDGE,"E11.29.5"),sQuery(id+"F0.wireOp",EDGE,"E11.29.6"),sQuery(id+"F0.wireOp",EDGE,"E11.29.7"),sQuery(id+"F0.wireOp",EDGE,"E11.29.8"),sQuery(id+"F0.wireOp",EDGE,"E11.29.9"),sQuery(id+"F0.wireOp",EDGE,"E12.trimOffspring"),sQuery(id+"F0.wireOp",EDGE,"E13.trimOffspring"),sQuery(id+"F0.wireOp",EDGE,"E14.trimOffspring"),sQuery(id+"F0.wireOp",EDGE,"E15.trimOffspring"),sQuery(id+"F0.wireOp",EDGE,"E16.trimOffspring"),sQuery(id+"F0.wireOp",EDGE,"E17.trimOffspring"),sQuery(id+"F0.wireOp",EDGE,"E18.trimOffspring"),sQuery(id+"F0.wireOp",EDGE,"E19.trimOffspring"),sQuery(id+"F0.wireOp",EDGE,"E20.trimOffspring"),sQuery(id+"F0.wireOp",EDGE,"E21.trimOffspring"),sQuery(id+"F0.wireOp",EDGE,"E22.trimOffspring"),sQuery(id+"F0.wireOp",EDGE,"E23.trimOffspring"),sQuery(id+"F0.wireOp",EDGE,"E24.trimOffspring"),sQuery(id+"F0.wireOp",EDGE,"E25.trimOffspring"),sQuery(id+"F0.wireOp",EDGE,"E26.trimOffspring"),sQuery(id+"F0.wireOp",EDGE,"E27.trimOffspring"),sQuery(id+"F0.wireOp",EDGE,"E28.trimOffspring"),sQuery(id+"F0.wireOp",EDGE,"E29.trimOffspring"),sQuery(id+"F0.wireOp",EDGE,"E30.trimOffspring"),sQuery(id+"F0.wireOp",EDGE,"E31.trimOffspring"),sQuery(id+"F0.wireOp",EDGE,"E32.trimOffspring"),sQuery(id+"F0.wireOp",EDGE,"E33.trimOffspring"),sQuery(id+"F0.wireOp",EDGE,"E34.trimOffspring"),sQuery(id+"F0.wireOp",EDGE,"E35.trimOffspring"),sQuery(id+"F0.wireOp",EDGE,"E36.trimOffspring"),sQuery(id+"F0.wireOp",EDGE,"E37.trimOffspring"),sQuery(id+"F0.wireOp",EDGE,"E38.trimOffspring"),sQuery(id+"F0.wireOp",EDGE,"E39.trimOffspring")])],"isStart":false});
            var sketch = newSketch(context, id + "F2", { "sketchPlane" : qUnion([Q0])});
            skCircle(sketch, "E41", {"center": v(0, 0) * mm, "radius": 6.35 * mm});
            skCircle(sketch, "E42", {"center": v(0, 0) * mm, "radius": 12.7 * mm});
            skSolve(sketch);
        }
        {
            var Q0;
            Q0 = qSketchRegion(id + "F2", true);
            extrude(context, id + "F3", {"entities" : qUnion([Q0]), "operationType" : NewBodyOperationType.ADD, "depth" : 12.7 * mm});
        }
    });
